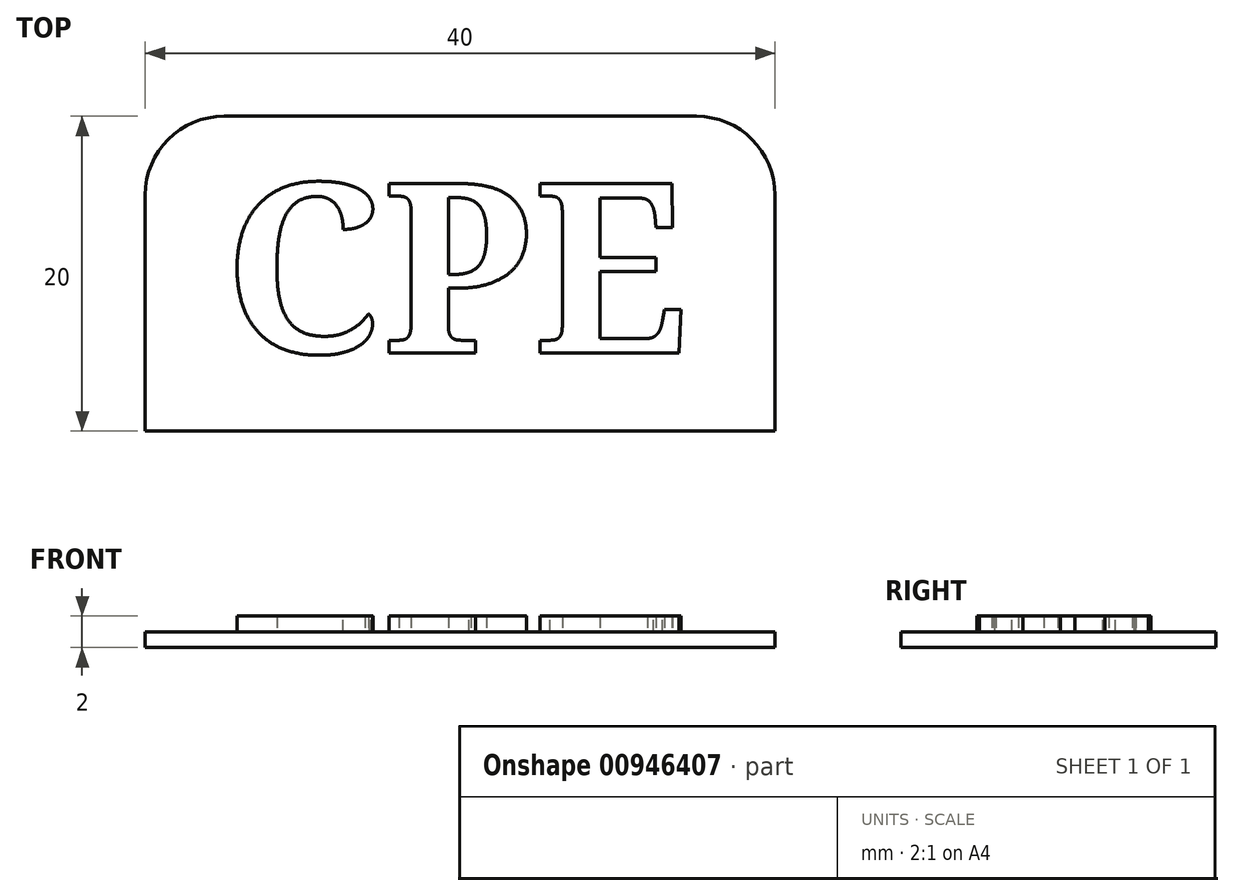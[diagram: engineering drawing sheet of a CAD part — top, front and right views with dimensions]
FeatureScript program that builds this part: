
annotation { "Feature Type Name" : "Feature", "Feature Type Description" : "" }
export const myFeature = defineFeature(function(context is Context, id is Id, definition is map)
    precondition{}
    {
        {
            var Q0;
            Q0=qCreatedBy(makeId("Top.planeOp"),FACE);
            var sketch = newSketch(context, id + "F0", { "sketchPlane" : qUnion([Q0])});
            skLineSegment(sketch, "E0.bottom", {"start": v(-20, 10) * mm, "end": v(20, 10) * mm});
            skLineSegment(sketch, "E0.top", {"start": v(-20, -10) * mm, "end": v(20, -10) * mm});
            skLineSegment(sketch, "E0.left", {"start": v(-20, 10) * mm, "end": v(-20, -10) * mm});
            skLineSegment(sketch, "E0.right", {"start": v(20, 10) * mm, "end": v(20, -10) * mm});
            skPoint(sketch, "E0.middle", {"position": v(0, 0) * mm});
            skSolve(sketch);
        }
        {
            var Q0;
            Q0=makeQuery(id+"F0.imprint","IMPRINT",FACE,{"disambiguationData":[TD([[makeQuery(id+"F0.imprint","IMPRINT",EDGE,{"derivedFrom":sQuery(id+"F0.wireOp",EDGE,"E0.bottom")}),-1.0]])]});
            extrude(context, id + "F1", {"entities" : qUnion([Q0]), "depth" : 1 * mm, "offsetDistance" : 25 * mm});
        }
        {
            var Q0;
            Q0=makeQuery(id+"F1.opExtrude","CAP_FACE",FACE,{"disambiguationData":[OSD([sQuery(id+"F0.wireOp",EDGE,"E0.bottom"),sQuery(id+"F0.wireOp",EDGE,"E0.top"),sQuery(id+"F0.wireOp",EDGE,"E0.left"),sQuery(id+"F0.wireOp",EDGE,"E0.right")])],"isStart":false});
            var sketch = newSketch(context, id + "F2", { "sketchPlane" : qUnion([Q0])});
            skText(sketch, "E1", { "text": "CPE", "fontName": "NotoSerif-Bold.ttf"});
            const initialGuessF2  = {"E1": [-0.015, -0.00503, 1, 0, 0.01084]};
            skSetInitialGuess(sketch, initialGuessF2);
            skSolve(sketch);
        }
        {
            var Q0;
            Q0=qSketchRegion(id+"F2",true);
            extrude(context, id + "F3", {"entities" : qUnion([Q0]), "operationType" : NewBodyOperationType.ADD, "depth" : 1 * mm, "offsetDistance" : 25 * mm});
        }
        {
            var Q0;
            Q0=makeQuery(id+"F1.opExtrude","SWEPT_EDGE",EDGE,{"disambiguationData":[OSD([sQuery(id+"F0.wireOp",EDGE,"E0.bottom"),sQuery(id+"F0.wireOp",EDGE,"E0.left")])]});
            var Q1;
            Q1=makeQuery(id+"F1.opExtrude","SWEPT_EDGE",EDGE,{"disambiguationData":[OSD([sQuery(id+"F0.wireOp",EDGE,"E0.bottom"),sQuery(id+"F0.wireOp",EDGE,"E0.right")])]});
            fillet(context, id + "F4", {"entities" : qUnion([Q0, Q1]), "radius" : 5 * mm, "tangentPropagation" : true, "allowEdgeOverflow" : false});
        }
    });
